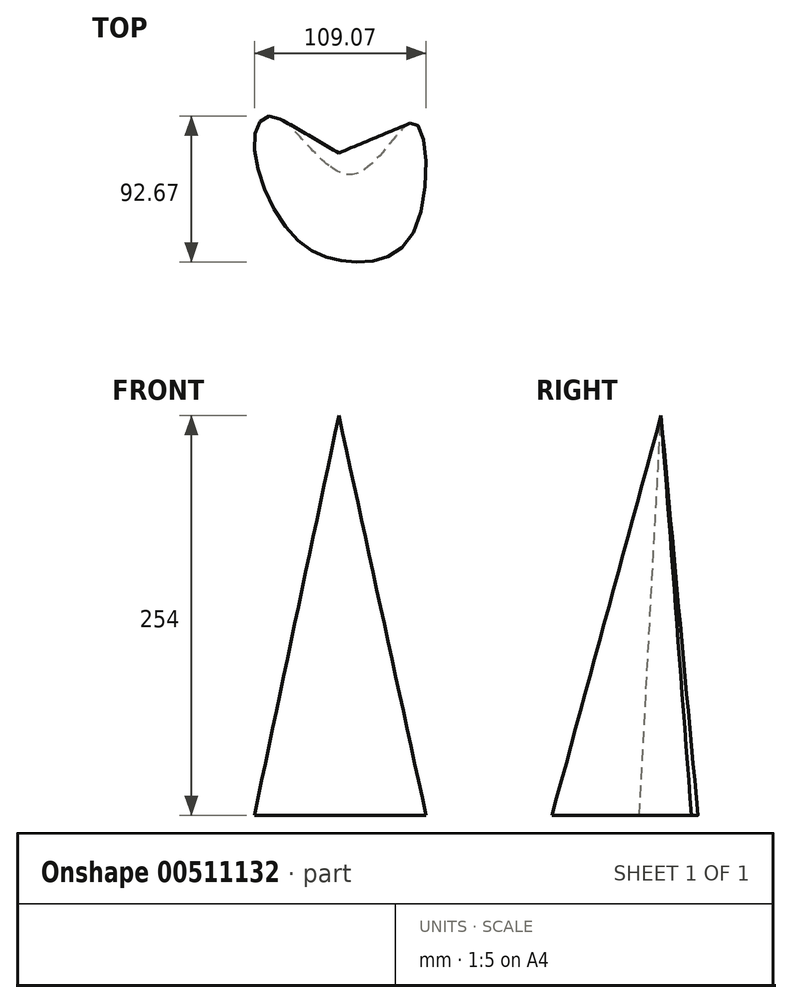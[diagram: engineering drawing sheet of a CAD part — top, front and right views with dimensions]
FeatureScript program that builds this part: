
annotation { "Feature Type Name" : "Feature", "Feature Type Description" : "" }
export const myFeature = defineFeature(function(context is Context, id is Id, definition is map)
    precondition{}
    {
        {
            var Q0;
            Q0=qCreatedBy(makeId("Top.planeOp"),FACE);
            var sketch = newSketch(context, id + "F0", { "sketchPlane" : qUnion([Q0])});
            skFitSpline(sketch, "E0", {"points": [v(-61.74, 38.75) * mm, v(-40.1, -24.25) * mm, v(0, -43.37) * mm, v(39.51, -23) * mm, v(38.57, 45.02) * mm, v(0, 12.11) * mm, v(-47.32, 48.16) * mm, v(-61.74, 38.75) * mm]});
            skSolve(sketch);
        }
        {
            var Q0;
            Q0=qCreatedBy(makeId("Top.planeOp"),FACE);
            cPlane(context, id + "F1", {"entities" : qUnion([Q0]), "cplaneType" : CPlaneType.OFFSET, "offset" : 254 * mm, "width" : 152.4 * mm, "height" : 152.4 * mm});
        }
        {
            var Q0;
            Q0=qCreatedBy(id+"F1.planeOp",FACE);
            var sketch = newSketch(context, id + "F2", { "sketchPlane" : qUnion([Q0])});
            skPoint(sketch, "E1", {"position": v(-8.74, 25.8) * mm});
            skSolve(sketch);
        }
        {
            var Q0;
            Q0=sQuery(id+"F2.wireOp",VERTEX,"E1");
            var Q1;
            Q1=makeQuery(id+"F0.imprint","IMPRINT",FACE,{"disambiguationData":[TD([[makeQuery(id+"F0.imprint","IMPRINT",EDGE,{"derivedFrom":sQuery(id+"F0.wireOp",EDGE,"E0")}),1.0]])]});
            loft(context, id + "F3", {"sheetProfilesArray" : [{ "sheetProfileEntities" : qUnion([Q0]) }, { "sheetProfileEntities" : qUnion([Q1]) }]});
        }
    });
